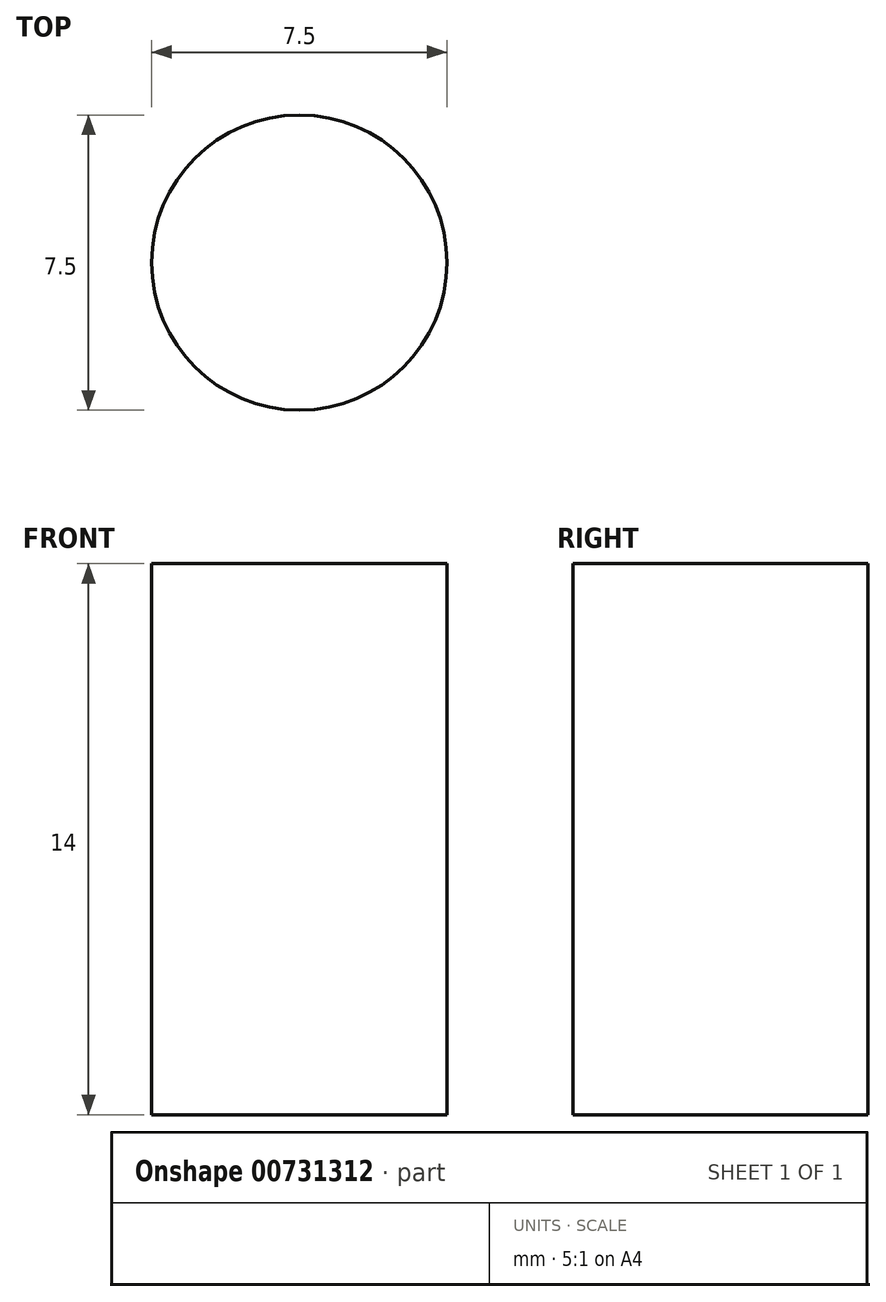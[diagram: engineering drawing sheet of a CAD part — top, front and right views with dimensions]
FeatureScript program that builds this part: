
annotation { "Feature Type Name" : "Feature", "Feature Type Description" : "" }
export const myFeature = defineFeature(function(context is Context, id is Id, definition is map)
    precondition{}
    {
        {
            var Q0;
            Q0=qCreatedBy(makeId("Top.planeOp"),FACE);
            var sketch = newSketch(context, id + "F0", { "sketchPlane" : qUnion([Q0])});
            skCircle(sketch, "E0", {"center": v(0, 0) * mm, "radius": 3.75 * mm});
            skSolve(sketch);
        }
        {
            var Q0;
            Q0=makeQuery(id+"F0.imprint","IMPRINT",FACE,{"disambiguationData":[TD([[makeQuery(id+"F0.imprint","IMPRINT",EDGE,{"derivedFrom":sQuery(id+"F0.wireOp",EDGE,"E0")}),1.0]])]});
            extrude(context, id + "F1", {"entities" : qUnion([Q0]), "depth" : 14 * mm, "offsetDistance" : 25 * mm});
        }
    });
